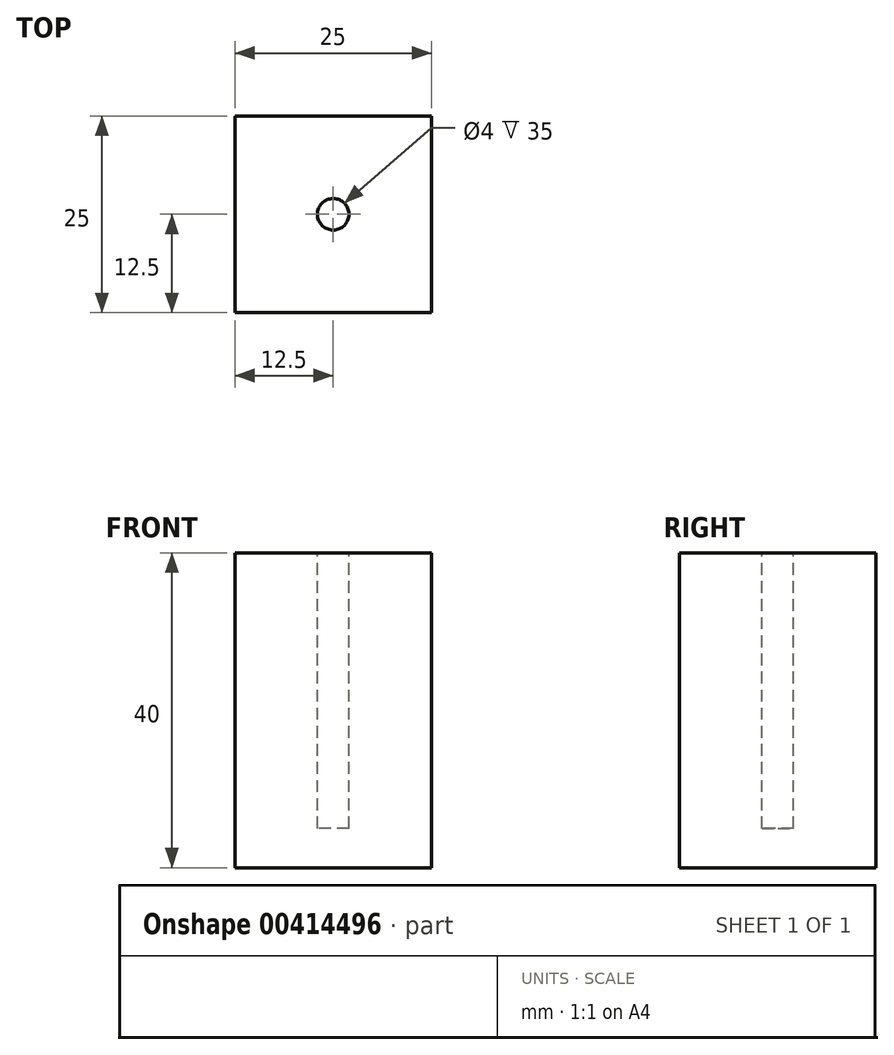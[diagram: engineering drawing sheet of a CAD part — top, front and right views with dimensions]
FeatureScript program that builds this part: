
annotation { "Feature Type Name" : "Feature", "Feature Type Description" : "" }
export const myFeature = defineFeature(function(context is Context, id is Id, definition is map)
    precondition{}
    {
        {
            var Q0;
            Q0=qCreatedBy(makeId("Top.planeOp"),FACE);
            var sketch = newSketch(context, id + "F0", { "sketchPlane" : qUnion([Q0])});
            skLineSegment(sketch, "E0.bottom", {"start": v(0, 0) * mm, "end": v(25, 0) * mm});
            skLineSegment(sketch, "E0.top", {"start": v(0, 25) * mm, "end": v(25, 25) * mm});
            skLineSegment(sketch, "E0.left", {"start": v(0, 0) * mm, "end": v(0, 25) * mm});
            skLineSegment(sketch, "E0.right", {"start": v(25, 0) * mm, "end": v(25, 25) * mm});
            skSolve(sketch);
        }
        {
            var Q0;
            Q0=makeQuery(id+"F0.imprint","IMPRINT",FACE,{"disambiguationData":[TD([[makeQuery(id+"F0.imprint","IMPRINT",EDGE,{"derivedFrom":sQuery(id+"F0.wireOp",EDGE,"E0.bottom")}),1.0]])]});
            extrude(context, id + "F1", {"entities" : qUnion([Q0]), "depth" : 40 * mm, "offsetDistance" : 25 * mm});
        }
        {
            var Q0;
            Q0=makeQuery(id+"F1.opExtrude","CAP_FACE",FACE,{"disambiguationData":[OSD([sQuery(id+"F0.wireOp",EDGE,"E0.bottom"),sQuery(id+"F0.wireOp",EDGE,"E0.top"),sQuery(id+"F0.wireOp",EDGE,"E0.left"),sQuery(id+"F0.wireOp",EDGE,"E0.right")])],"isStart":false});
            var sketch = newSketch(context, id + "F2", { "sketchPlane" : qUnion([Q0])});
            skCircle(sketch, "E1", {"center": v(12.5, 12.5) * mm, "radius": 2 * mm});
            skPoint(sketch, "E1.centerSnap0", {"position": v(12.5, 25) * mm});
            skLineSegment(sketch, "E2", {"start": v(0, 12.5) * mm, "end": v(25, 12.5) * mm, "construction": true});
            skLineSegment(sketch, "E3", {"start": v(12.5, 25) * mm, "end": v(12.5, 0) * mm, "construction": true});
            skSolve(sketch);
        }
        {
            var Q0;
            Q0 = qSketchRegion(id + "F2", true);
            extrude(context, id + "F3", {"entities" : qUnion([Q0]), "operationType" : NewBodyOperationType.REMOVE, "oppositeDirection" : true, "depth" : 35 * mm, "offsetDistance" : 25 * mm});
        }
    });
